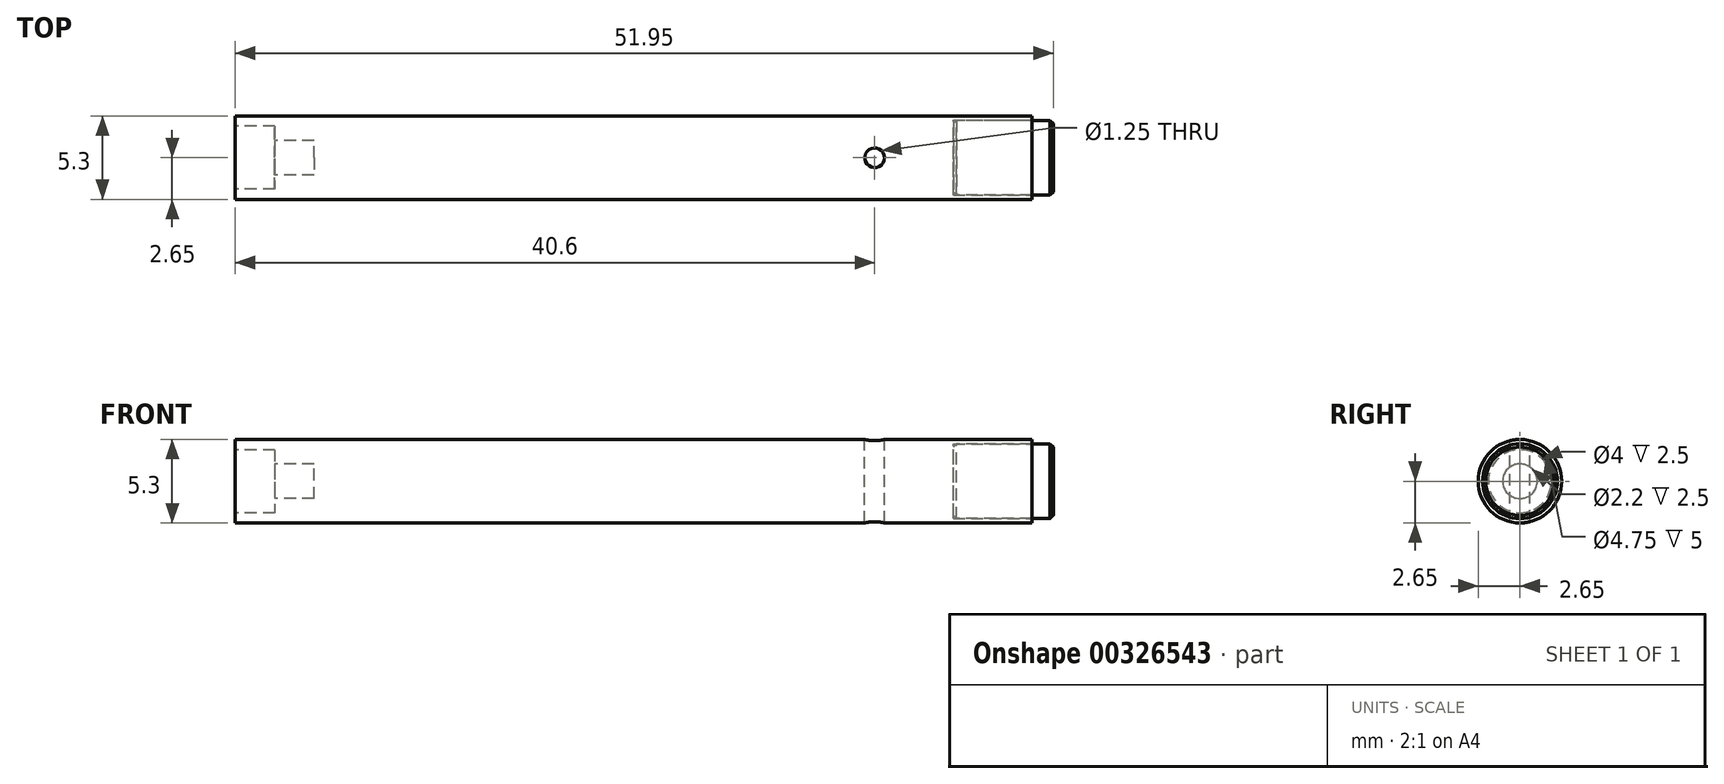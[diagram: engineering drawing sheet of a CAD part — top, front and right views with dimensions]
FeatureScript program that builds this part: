
annotation { "Feature Type Name" : "Feature", "Feature Type Description" : "" }
export const myFeature = defineFeature(function(context is Context, id is Id, definition is map)
    precondition{}
    {
        {
            var Q0;
            Q0=qCreatedBy(makeId("Right.planeOp"),FACE);
            var sketch = newSketch(context, id + "F0", { "sketchPlane" : qUnion([Q0])});
            skCircle(sketch, "E0", {"center": v(0, 0) * mm, "radius": 2.65 * mm});
            skSolve(sketch);
        }
        {
            var Q0;
            Q0=makeQuery(id+"F0.imprint","IMPRINT",FACE,{"disambiguationData":[TD([[makeQuery(id+"F0.imprint","IMPRINT",EDGE,{"derivedFrom":sQuery(id+"F0.wireOp",EDGE,"E0")}),1.0]])]});
            extrude(context, id + "F1", {"entities" : qUnion([Q0]), "depth" : 50.6 * mm});
        }
        {
            var Q0;
            Q0=qCreatedBy(makeId("Right.planeOp"),FACE);
            var sketch = newSketch(context, id + "F2", { "sketchPlane" : qUnion([Q0])});
            skCircle(sketch, "E1", {"center": v(0, 0) * mm, "radius": 1.1 * mm});
            skSolve(sketch);
        }
        {
            var Q0;
            Q0=qSketchRegion(id+"F2",true);
            extrude(context, id + "F3", {"entities" : qUnion([Q0]), "operationType" : NewBodyOperationType.REMOVE, "depth" : 5 * mm});
        }
        {
            var Q0;
            Q0=qCreatedBy(makeId("Top.planeOp"),FACE);
            var sketch = newSketch(context, id + "F4", { "sketchPlane" : qUnion([Q0])});
            skCircle(sketch, "E2", {"center": v(40.6, 0) * mm, "radius": 0.62 * mm});
            skSolve(sketch);
        }
        {
            var Q0;
            Q0=qSketchRegion(id+"F4",true);
            extrude(context, id + "F5", {"entities" : qUnion([Q0]), "operationType" : NewBodyOperationType.REMOVE, "oppositeDirection" : true, "depth" : 25 * mm, "symmetric" : true});
        }
        {
            var Q0;
            Q0=makeQuery(id+"F1.opExtrude","CAP_FACE",FACE,{"disambiguationData":[OSD([sQuery(id+"F0.wireOp",EDGE,"E0")])],"isStart":true});
            var sketch = newSketch(context, id + "F6", { "sketchPlane" : qUnion([Q0])});
            skCircle(sketch, "E3", {"center": v(0, 0) * mm, "radius": 2 * mm});
            skSolve(sketch);
        }
        {
            var Q0;
            Q0=qSketchRegion(id+"F6",true);
            extrude(context, id + "F7", {"entities" : qUnion([Q0]), "operationType" : NewBodyOperationType.REMOVE, "oppositeDirection" : true, "depth" : 2.5 * mm});
        }
        {
            var Q0;
            Q0=makeQuery(id+"F1.opExtrude","CAP_FACE",FACE,{"disambiguationData":[OSD([sQuery(id+"F0.wireOp",EDGE,"E0")])],"isStart":false});
            var sketch = newSketch(context, id + "F8", { "sketchPlane" : qUnion([Q0])});
            skCircle(sketch, "E4", {"center": v(0, 0) * mm, "radius": 2.38 * mm});
            skSolve(sketch);
        }
        {
            var Q0;
            Q0 = qSketchRegion(id + "F8", true);
            extrude(context, id + "F9", {"entities" : qUnion([Q0]), "operationType" : NewBodyOperationType.REMOVE, "oppositeDirection" : true, "depth" : 5 * mm});
        }
        {
            var Q0;
            Q0=makeQuery(id+"F9.boolean.opBoolean","COPY",FACE,{"derivedFrom":makeQuery(id+"F9.opExtrude","CAP_FACE",FACE,{"disambiguationData":[OSD([sQuery(id+"F8.wireOp",EDGE,"E4")])],"isStart":false})});
            var sketch = newSketch(context, id + "F10", { "sketchPlane" : qUnion([Q0])});
            skCircle(sketch, "E5", {"center": v(0, 0) * mm, "radius": 2.37 * mm});
            skSolve(sketch);
        }
        {
            var Q0;
            Q0 = qSketchRegion(id + "F10", true);
            extrude(context, id + "F11", {"entities" : qUnion([Q0]), "depth" : 6.35 * mm});
        }
        {
            var Q0;
            Q0=makeQuery(id+"F11.opExtrude","CAP_EDGE",EDGE,{"disambiguationData":[OSD([sQuery(id+"F10.wireOp",EDGE,"E5")])],"isStart":false});
            var Q1;
            Q1=makeQuery(id+"F11.opExtrude","CAP_EDGE",EDGE,{"disambiguationData":[OSD([sQuery(id+"F10.wireOp",EDGE,"E5")])],"isStart":true});
            chamfer(context, id + "F12", {"entities" : qUnion([Q0, Q1]), "width" : .2 * mm, "tangentPropagation" : true});
        }
    });
